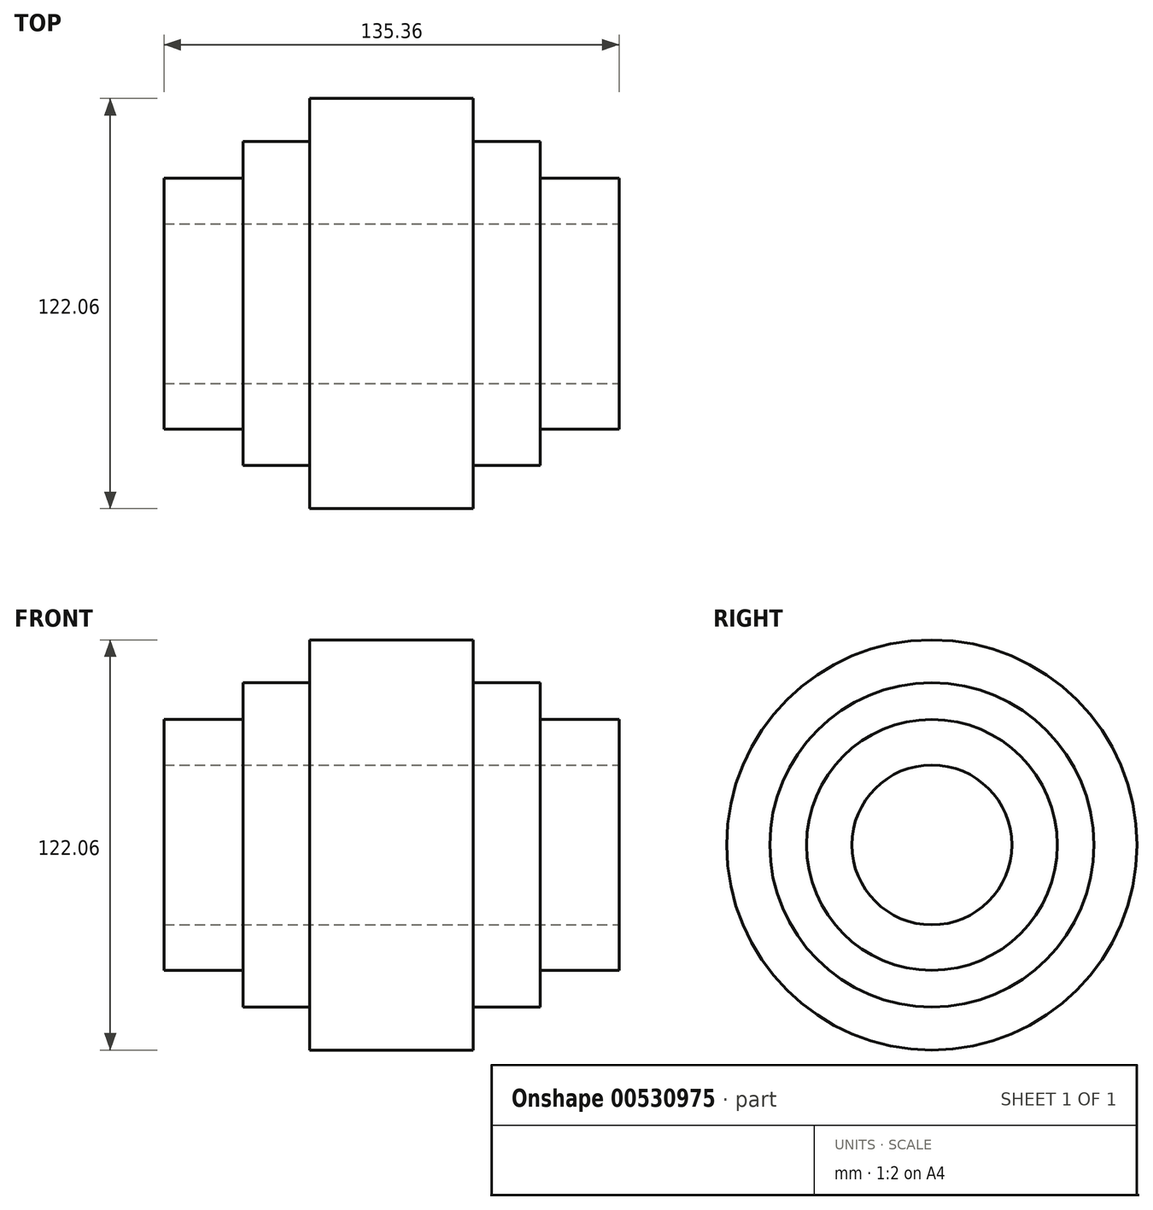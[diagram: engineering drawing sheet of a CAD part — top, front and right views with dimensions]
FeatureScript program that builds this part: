
annotation { "Feature Type Name" : "Feature", "Feature Type Description" : "" }
export const myFeature = defineFeature(function(context is Context, id is Id, definition is map)
    precondition{}
    {
        {
            var Q0;
            Q0=qCreatedBy(makeId("Front.planeOp"),FACE);
            var sketch = newSketch(context, id + "F0", { "sketchPlane" : qUnion([Q0])});
            skLineSegment(sketch, "E0", {"start": v(0, 61.03) * mm, "end": v(24.32, 61.03) * mm});
            skLineSegment(sketch, "E1", {"start": v(24.32, 61.03) * mm, "end": v(24.32, 48.21) * mm});
            skLineSegment(sketch, "E2", {"start": v(24.32, 48.21) * mm, "end": v(44.23, 48.21) * mm});
            skLineSegment(sketch, "E3", {"start": v(44.23, 48.21) * mm, "end": v(44.23, 37.3) * mm});
            skLineSegment(sketch, "E4", {"start": v(44.23, 37.3) * mm, "end": v(67.68, 37.3) * mm});
            skLineSegment(sketch, "E5", {"start": v(67.68, 37.3) * mm, "end": v(67.68, 23.79) * mm});
            skLineSegment(sketch, "E6", {"start": v(67.68, 23.79) * mm, "end": v(0, 23.79) * mm});
            skLineSegment(sketch, "E7", {"start": v(0, 23.79) * mm, "end": v(0, 61.03) * mm});
            skLineSegment(sketch, "E8", {"start": v(-74.96, 22.03) * mm, "end": v(-74.98, 23.79) * mm, "construction": true});
            skLineSegment(sketch, "E9", {"start": v(-74.98, 23.79) * mm, "end": v(-74.96, 22.03) * mm, "construction": true});
            skLineSegment(sketch, "E10", {"start": v(44.46, 0) * mm, "end": v(-40.38, 0) * mm, "construction": true});
            skLineSegment(sketch, "E11.MirrorCS", {"start": v(0, 61.03) * mm, "end": v(-24.32, 61.03) * mm});
            skLineSegment(sketch, "E12.MirrorCS", {"start": v(-67.68, 23.79) * mm, "end": v(0, 23.79) * mm});
            skLineSegment(sketch, "E13.MirrorCS", {"start": v(-67.68, 37.3) * mm, "end": v(-67.68, 23.79) * mm});
            skLineSegment(sketch, "E14.MirrorCS", {"start": v(-44.23, 37.3) * mm, "end": v(-67.68, 37.3) * mm});
            skLineSegment(sketch, "E15.MirrorCS", {"start": v(-44.23, 48.21) * mm, "end": v(-44.23, 37.3) * mm});
            skLineSegment(sketch, "E16.MirrorCS", {"start": v(-24.32, 48.21) * mm, "end": v(-44.23, 48.21) * mm});
            skLineSegment(sketch, "E17.MirrorCS", {"start": v(-24.32, 61.03) * mm, "end": v(-24.32, 48.21) * mm});
            skSolve(sketch);
        }
        {
            var Q0;
            Q0 = qSketchRegion(id + "F0", true);
            var Q1;
            Q1=sQuery(id+"F0.wireOp",EDGE,"E10");
            revolve(context, id + "F1", {"entities" : qUnion([Q0]), "axis" : qUnion([Q1]), "revolveType" : RevolveType.FULL});
        }
    });
